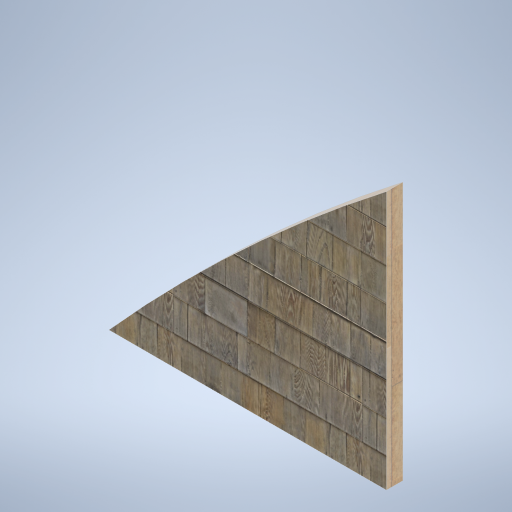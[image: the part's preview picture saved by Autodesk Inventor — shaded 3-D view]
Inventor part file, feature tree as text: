
AUTODESK INVENTOR PART (.ipt)
format: ipt  version: 2024.2 (Build 282272000, 272)  size: 367,104 bytes
history: native  units: mm
features: extrude x1, sketch x1
ambient origin geometry x8: Origin, YZ Plane, XZ Plane, XY Plane, X Axis, Y Axis, Z Axis, Center Point
bodies: Solid1 (feature_tree)
feature tree (2):
  extrude  "Extrusion1"  [1 undecoded]
  sketch  "Sketch1"  dims[d0=80.0mm d1=0.0mm]
note: 1 required parameter value undecoded (feature->parameter linkage not recoverable at this tier; creation-order binding heuristic only, values carry confidence <= 0.55)
